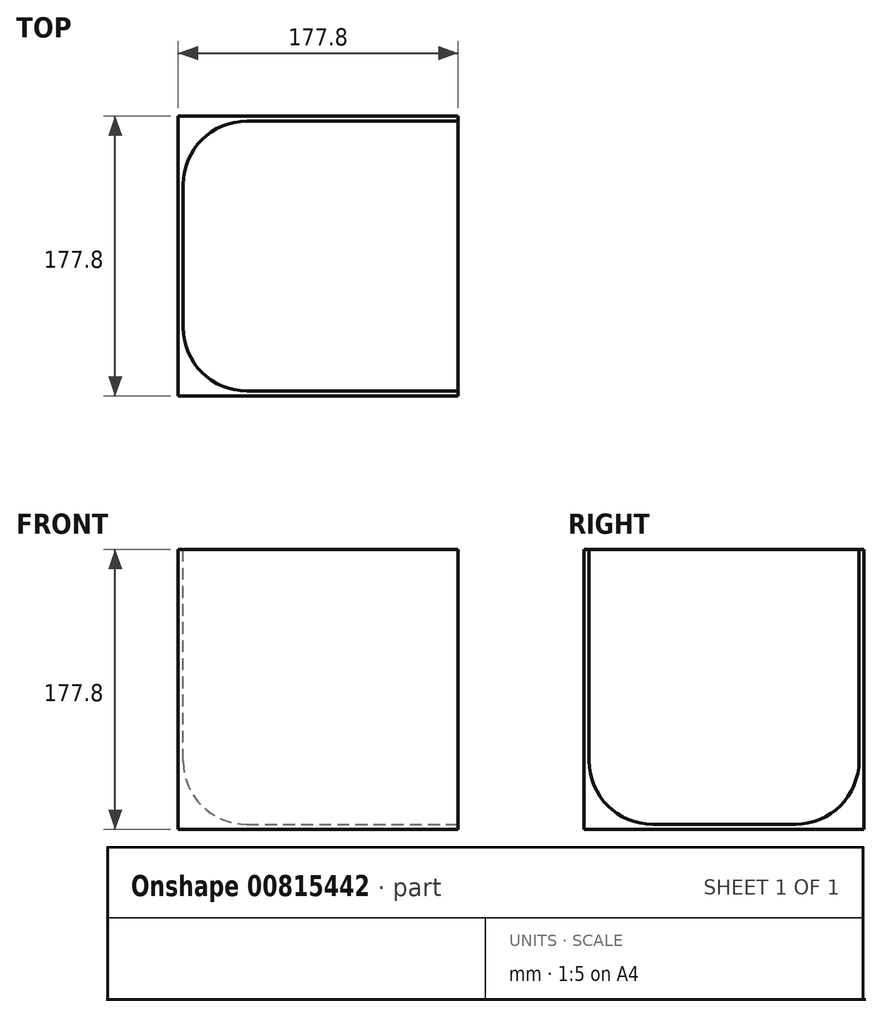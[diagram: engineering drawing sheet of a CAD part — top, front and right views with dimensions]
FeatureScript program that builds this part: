
annotation { "Feature Type Name" : "Feature", "Feature Type Description" : "" }
export const myFeature = defineFeature(function(context is Context, id is Id, definition is map)
    precondition{}
    {
        {
            var Q0;
            Q0=qCreatedBy(makeId("Top.planeOp"),FACE);
            var sketch = newSketch(context, id + "F0", { "sketchPlane" : qUnion([Q0])});
            skLineSegment(sketch, "E0.bottom", {"start": v(88.9, -88.9) * mm, "end": v(-88.9, -88.9) * mm});
            skLineSegment(sketch, "E0.top", {"start": v(88.9, 88.9) * mm, "end": v(-88.9, 88.9) * mm});
            skLineSegment(sketch, "E0.left", {"start": v(88.9, -88.9) * mm, "end": v(88.9, 88.9) * mm});
            skLineSegment(sketch, "E0.right", {"start": v(-88.9, -88.9) * mm, "end": v(-88.9, 88.9) * mm});
            skPoint(sketch, "E0.middle", {"position": v(0, 0) * mm});
            skSolve(sketch);
        }
        {
            var Q0;
            Q0 = qSketchRegion(id + "F0", true);
            extrude(context, id + "F1", {"entities" : qUnion([Q0]), "depth" : 177.8 * mm, "offsetDistance" : 25.4 * mm});
        }
        {
            var Q0;
            Q0=makeQuery(id+"F1.opExtrude","CAP_FACE",FACE,{"disambiguationData":[OSD([sQuery(id+"F0.wireOp",EDGE,"E0.bottom"),sQuery(id+"F0.wireOp",EDGE,"E0.top"),sQuery(id+"F0.wireOp",EDGE,"E0.left"),sQuery(id+"F0.wireOp",EDGE,"E0.right")])],"isStart":false});
            var sketch = newSketch(context, id + "F2", { "sketchPlane" : qUnion([Q0])});
            skLineSegment(sketch, "E1.bottom", {"start": v(-85.73, 85.73) * mm, "end": v(117.48, 85.73) * mm});
            skLineSegment(sketch, "E1.top", {"start": v(-85.72, -85.73) * mm, "end": v(117.48, -85.73) * mm});
            skLineSegment(sketch, "E1.left", {"start": v(-85.73, 85.73) * mm, "end": v(-85.72, -85.73) * mm});
            skLineSegment(sketch, "E1.right", {"start": v(117.48, 85.73) * mm, "end": v(117.48, -85.72) * mm});
            skSolve(sketch);
        }
        {
            var Q0;
            {var subQ0=sQuery(id+"F2.wireOp",EDGE,"E1.left");var subQ1=sQuery(id+"F2.wireOp",EDGE,"E1.bottom");var subQ2=makeQuery(id+"F2.imprint","INTERSECT",VERTEX,{"derivedFrom":[subQ1,subQ0]});Q0=makeQuery(id+"F2.imprint","IMPRINT",FACE,{"disambiguationData":[TD([[makeQuery(id+"F2.imprint","IMPRINT",EDGE,{"disambiguationData":[TD([[subQ2,-1.0]])],"derivedFrom":subQ1}),-1.0]])]});}
            var Q1;
            {var subQ2=sQuery(id+"F2.wireOp",EDGE,"E1.top");Q1=makeQuery(id+"F2.imprint","IMPRINT",FACE,{"disambiguationData":[TD([[makeQuery(id+"F2.imprint","IMPRINT",EDGE,{"derivedFrom":subQ2}),1.0]])]});}
            extrude(context, id + "F3", {"entities" : qUnion([Q0, Q1]), "operationType" : NewBodyOperationType.REMOVE, "oppositeDirection" : true, "depth" : 174.62 * mm, "offsetDistance" : 25.4 * mm});
        }
        {
            var Q0;
            Q0=makeQuery(id+"F3.boolean.opBoolean","COPY",EDGE,{"derivedFrom":makeQuery(id+"F3.opExtrude","CAP_EDGE",EDGE,{"disambiguationData":[OSD([sQuery(id+"F2.wireOp",EDGE,"E1.bottom")])],"isStart":false})});
            var Q1;
            Q1=makeQuery(id+"F3.boolean.opBoolean","COPY",EDGE,{"derivedFrom":makeQuery(id+"F3.opExtrude","SWEPT_EDGE",EDGE,{"disambiguationData":[OSD([sQuery(id+"F2.wireOp",EDGE,"E1.bottom"),sQuery(id+"F2.wireOp",EDGE,"E1.left")])]})});
            var Q2;
            Q2=makeQuery(id+"F3.boolean.opBoolean","COPY",EDGE,{"derivedFrom":makeQuery(id+"F3.opExtrude","CAP_EDGE",EDGE,{"disambiguationData":[OSD([sQuery(id+"F2.wireOp",EDGE,"E1.left")])],"isStart":false})});
            var Q3;
            Q3=makeQuery(id+"F3.boolean.opBoolean","COPY",EDGE,{"derivedFrom":makeQuery(id+"F3.opExtrude","SWEPT_EDGE",EDGE,{"disambiguationData":[OSD([sQuery(id+"F2.wireOp",EDGE,"E1.top"),sQuery(id+"F2.wireOp",EDGE,"E1.left")])]})});
            var Q4;
            Q4=makeQuery(id+"F3.boolean.opBoolean","COPY",EDGE,{"derivedFrom":makeQuery(id+"F3.opExtrude","CAP_EDGE",EDGE,{"disambiguationData":[OSD([sQuery(id+"F2.wireOp",EDGE,"E1.top")])],"isStart":false})});
            fillet(context, id + "F4", {"entities" : qUnion([Q0, Q1, Q2, Q3, Q4]), "radius" : 40.47 * mm, "tangentPropagation" : true, "allowEdgeOverflow" : false});
        }
    });
